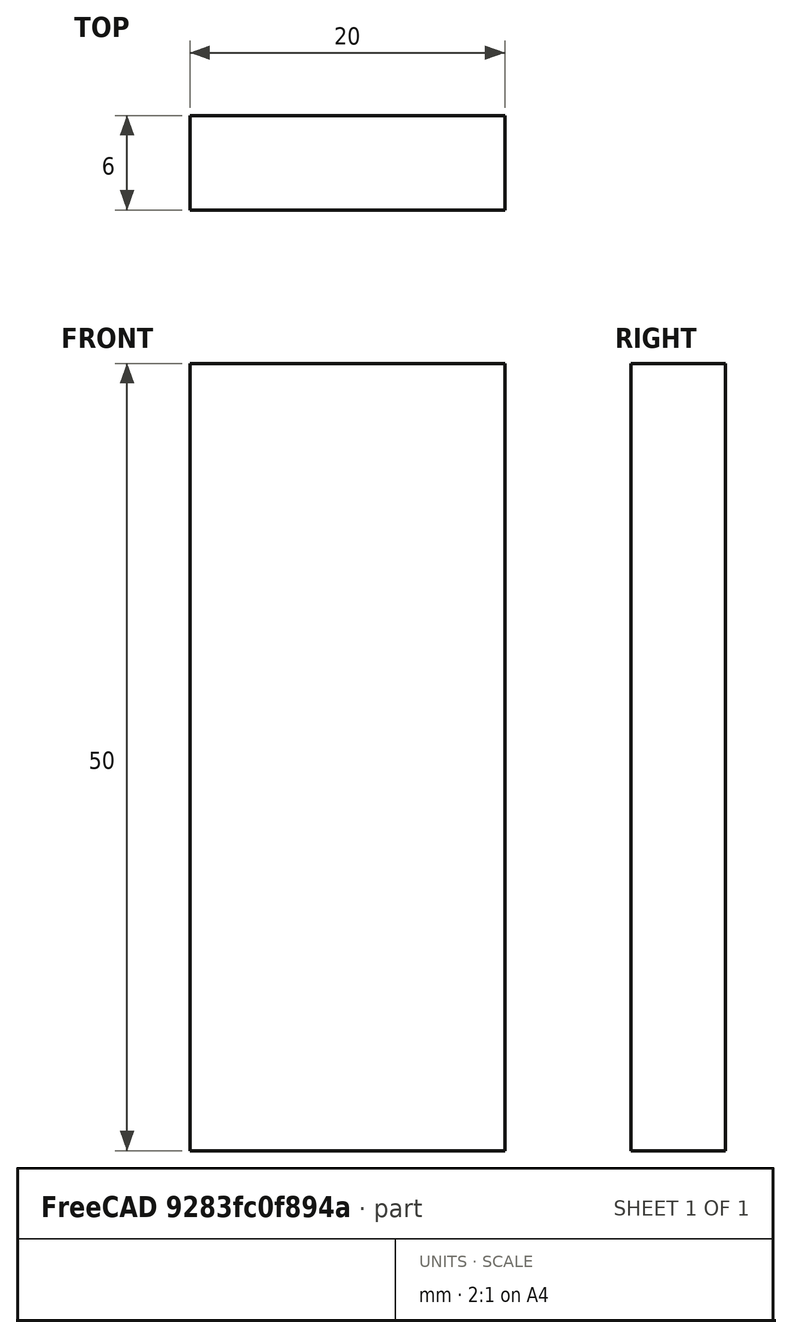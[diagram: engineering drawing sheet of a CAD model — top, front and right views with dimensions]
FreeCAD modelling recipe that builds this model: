
FCSTD DOCUMENT  (FreeCAD 0.15R4671 (Git))
Label: Flat Bar 20x6 EN10058 S235JR
License: All rights reserved
LicenseURL: http://en.wikipedia.org/wiki/All_rights_reserved
objects: Sketcher::SketchObject×1, Part::Extrusion×1
note: 2 computed .brp shape members not serialized (recipe doc carries the construction recipe); baked Part::Feature solids carry a one-line shape summary decoded from their .brp

FEATURE [Sketcher::SketchObject] Sketch
  sketch-geometry (4):
    g0: LineSegment StartX=-10 StartY=-3 StartZ=0 EndX=10 EndY=-3 EndZ=0
    g1: LineSegment StartX=10 StartY=-3 StartZ=0 EndX=10 EndY=3 EndZ=0
    g2: LineSegment StartX=10 StartY=3 StartZ=0 EndX=-10 EndY=3 EndZ=0
    g3: LineSegment StartX=-10 StartY=3 StartZ=0 EndX=-10 EndY=-3 EndZ=0
  constraints (12):
    c: Coincident(g0,g1)
    c: Coincident(g1,g2)
    c: Coincident(g2,g3)
    c: Coincident(g3,g0)
    c: Horizontal(g0)
    c: Horizontal(g2)
    c: Vertical(g1)
    c: Vertical(g3)
    c: Symmetric(g1,g2,g-2)
    c: Symmetric(g0,g1,g-1)
    c: DistanceY(g1) = 6
    c: DistanceX(g0) = 20
FEATURE [Part::Extrusion] Extrude  label="Flat Bar 20x6 EN10058 S235JR"
  Base = -> Sketch
  Dir = (0,0,50)
  Solid = true
